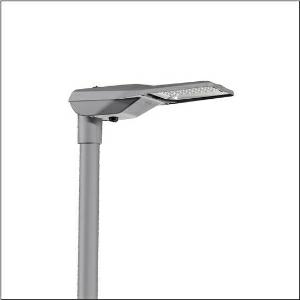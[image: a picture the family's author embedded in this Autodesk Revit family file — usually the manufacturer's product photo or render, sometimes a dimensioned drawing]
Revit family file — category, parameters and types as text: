
# Revit family: streetlight_sl_21_iq_mini___st0_8a_5xe2c31y08hb_5d56
name_source: partatom
category: Lighting Fixtures
units: mm (PartAtom-declared; Revit-internal decimal feet)

## family parameters
Cut with Voids When Loaded = No
Host = Face
Light Source = No
Part Type = Normal
Room Calculation Point = No
Round Connector Dimension = Use Diameter
Shared = No

## types (1)
- --- (1 x LED, 9750 lm, 71 W, 3000K)
    Apparent Load = 71 VA
    CIE Flux Codes = 38 75 97 100 100
    Color Rendering = 70
    Color Temperature = 3000K
    Default Elevation = 1800 mm
    Description = Streetlight SL 21 iQ mini, mast luminaire, primary light control with lens, of PMMA, primary optical cover: cover, of toughened safety glass, transparent, light distribution: ST0.8a, light emission: direct distribution, primary light characteristic: asymmetric, installation type: post-top, side-entry, LED, High Power LED, rated luminous flux: 9.750lm, luminous efficacy: 137lm/W, light colour: 730, colour temperature: 3000K, control gear: iQ-Street Remote, D4i with power reduction, control: pre-setting: logarithmic dimming characteristic, Street-Remote, Auto-Match, Temp-Guard, Lumen-Switch, Night-Set, Smart-Wire, Light-Fading, Desk-Remote (wireless, voltage-free reading and setting of iQ features in the workshop via application-optimized NFC function/RFID function), optimised constant luminous flux control (CLO 2.0), mains connection: 220..240V, AC, 50/60Hz, start of lifetime: 71W, end of service life: 75W, reduction: 30W, luminaire housing, of diecast aluminium, powder-coated, SITECO metallic grey (DB 702S), corrosivity category C5 high according to DIN EN ISO 12944, please order mast flange separately, inclination adjustable: 0°, 5°, 10°, 15°, sealing non-destructively replaceable, multi-level sealing system, length: 628mm, width: 235mm, height: 110mm, mast flange for spigot size: 42mm (side-entry): 5XC10008XM4, 60/48mm (side-entry/post-top): 5XC10108XM2, 76/60mm (side-entry/post-top): 5XC10108XM1, mounting height: 4..8m, Smart Interface below and above, protection rating (complete): IP66, insulation class (complete): insulation class II (safety insulation), certification: CE, ENEC, ENEC+, VDE, impact resistance: IK10, permissible operating ambient temperature for outdoor applications: -40..+50°C, standard-compliant lighting for roads and squares, packaging unit: 1 piece

Light Distribution: ST0.8a
    Height = 110 mm
    Lamp = 1 x LED
    Lamp Light Flux = 9750 lm
    Lamp Power = 71 W
    Lamp count = 1
    Length = 625 mm
    Luminous efficacy = 137 lm/W
    Manufacturer = Siteco
    ModVariant = No
    Model = 5XE2C31Y08HB
    Number of Poles = 1
    OnlyDefault = Yes
    Power Factor = 1
    Product Name = Streetlight SL 21 iQ mini | ST0.8a
    Product group = mast luminaire | pylon top
    ProductGroupID = 6100
    Protection Class = Protection class II
    Protection Degree = IP 66
    RLX_Detail_Level = 1
    RLX_Emergency_Light_Flux = 0 lm
    RLX_Emergency_Type = 0
    RLX_Emergency_Type_DB = No
    RlxData = <blob elided: 94061 chars, md5=14c09780>
    Socket = socket
    Standby Power = 0 W
    System Light Flux = 9750 lm
    System Power = 71 W
    Type Comments = factory setting: luminous flux: 100 % | dim-lin: 254 | 716 mA
    Type Image = l_1003514.jpg
    URL = http://relux.com
    VarID = @adj_113431
    Voltage = 0 V
    Weight = 0.00 kg
    Width = 234 mm

## geometry (parser evidence)
native form markers: Blend x4, Sweep x12
no freeform markers — native parametric forms only
